# Revit family: ASSA_ABLOY_VersaMax_Touchless_OHC_FBO03
name_source: partatom
category: Doors
units: mm (PartAtom-declared; Revit-internal decimal feet)

## family parameters
Always vertical = Yes
Cut with Voids When Loaded = No
Host = Wall
OmniClass Number = 23.30.10.00
OmniClass Title = Doors
Room Calculation Point = No
Shared = No

## types (3) — shared parameters
Analytic Construction = <None>
BIMobject category = Sliding Doors
Bottom Profile Height = Fix Leaf1 : 0'4''
Bottom Profile Option 01 = Fix Leaf1 : 0'4''
Bottom Profile Option 02 = Fix Leaf1 : 0'7''
Bottom Profile Option 03 = Fix Leaf1 : 0'10''
Brass Polished Finish = Brass, Polished
Brass Satin Finish = Brass, Satin
Clear Anodized = Clear Anodized
Dark Bronze Anodized = Dark Bronze Anodized
Date of publishing = 2015-02-23
Depth = 0.00
Edition number = 1
Frame Material = Clear Anodized
Function = Interior
Gap = 6.35 mm  [stored 0.0208333 ft]
Glass = Glass
Height = 2279.65 mm  [stored 7.47917 ft]
IFC Classification = Door
Leaf Height = 2155.83 mm
Manufacturer name = ASSA ABLOY Entrance Systems-North America
Material main = Aluminium
NBS Reference Code = 25-30-20-77
NBS Reference Description = Sliding Doorset Systems
Nominal height = 0.00
Nominal width = 0.00
Product SKU = VersaMax_Tele_Touchless_OHC
Product data url = http://besam-na.bimobject.com
Product family = ICU
Product group = Touchless
QR code = http://besam-na.bimobject.com
Rough Height = 2286 mm  [stored 7.5 ft]
Stainless Steel Polished Finish = Stainless Steel, Polished
Stainless Steel Satin Finish = Stainless Steel, Satin
Thickness = 152.4 mm  [stored 0.5 ft]
Top Profile Height = 101.6 mm  [stored 0.333333 ft]
UNSPSC Code = 301715
Uniclass 1.4 Code = L4133
Uniclass 1.4 Description = Sliding
Uniclass 2.0 Code = SS-25-30-20-77
Uniclass 2.0 Description = Sliding Doorset Systems
Wall Closure = By host
Weight Net (Kg) = 0

## per-type parameters (varying)
| type | Leaf Width | Mid Leaf Position | Rough Width | Width |
| ICU-TE-3FSL-8 | 827.09 mm | 1584.33 mm | 2451.1 mm  [stored 8.04167 ft] | 2438.4 mm  [stored 8 ft] |
| ICU-TE-3FSL-10 | 1030.29 mm | 1990.73 mm | 3060.7 mm  [stored 10.0417 ft] | 3048 mm  [stored 10 ft] |
| ICU-TE-3FSL-12 | 1233.49 mm | 2397.13 mm | 3670.3 mm  [stored 12.0417 ft] | 3657.6 mm  [stored 12 ft] |

note: [stored X ft] marks values corroborated as IEEE doubles in the binary element streams (Revit-internal decimal feet)

## geometry (parser evidence)
native form markers: Blend x2, Sweep x33
no freeform markers — native parametric forms only
